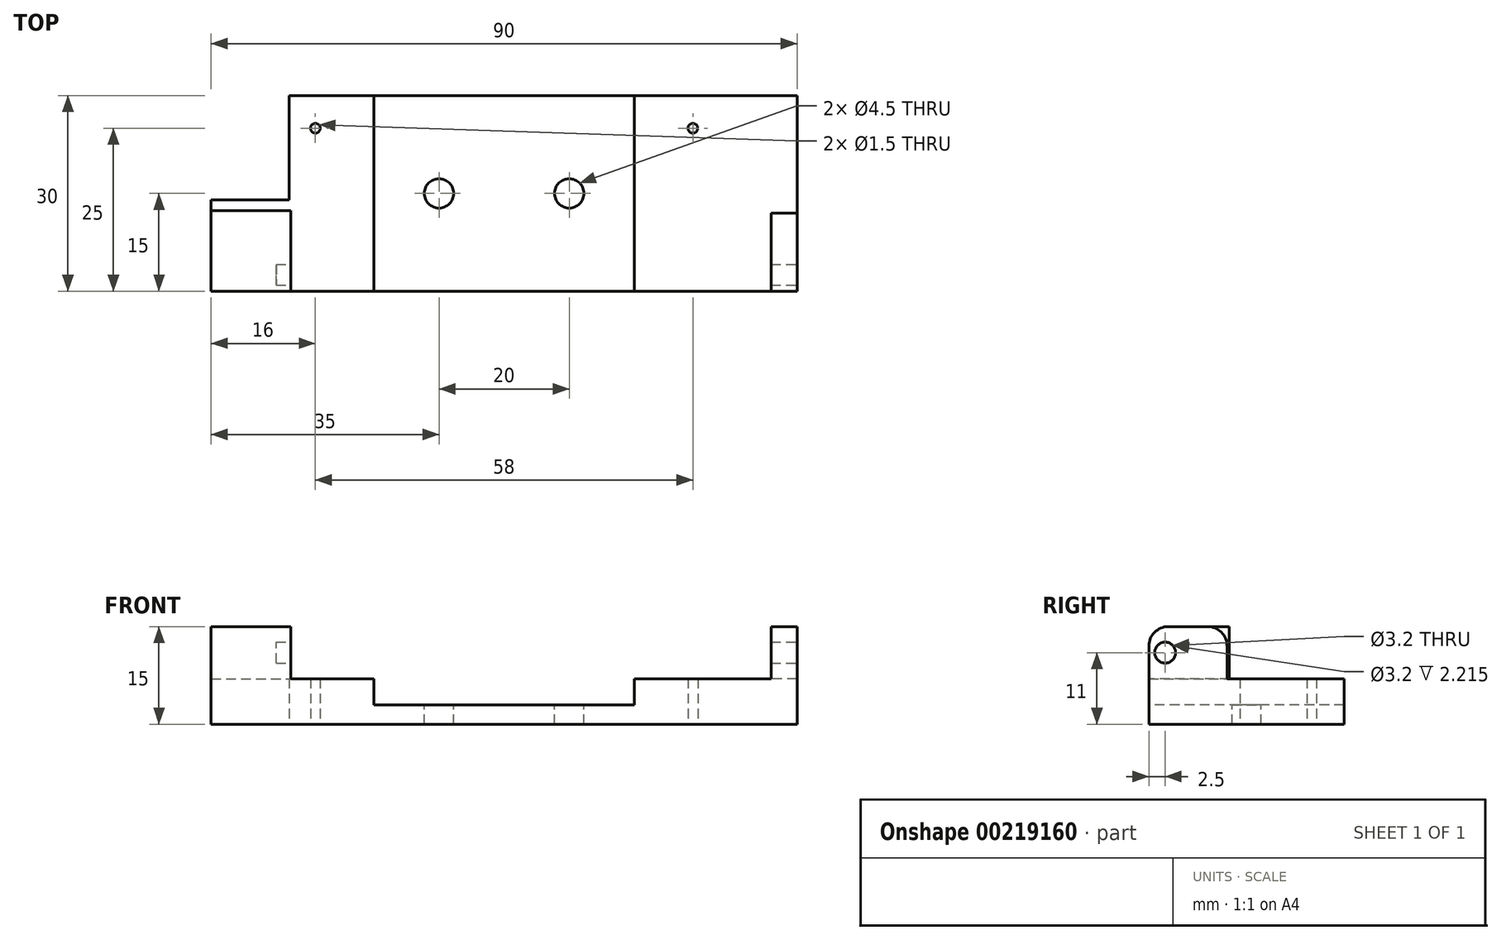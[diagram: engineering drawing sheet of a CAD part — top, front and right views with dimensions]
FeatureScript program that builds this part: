
annotation { "Feature Type Name" : "Feature", "Feature Type Description" : "" }
export const myFeature = defineFeature(function(context is Context, id is Id, definition is map)
    precondition{}
    {
        {
            var Q0;
            Q0=qCreatedBy(makeId("Top.planeOp"),FACE);
            var sketch = newSketch(context, id + "F0", { "sketchPlane" : qUnion([Q0])});
            skLineSegment(sketch, "E0.bottom", {"start": v(-45, 15) * mm, "end": v(45, 15) * mm});
            skLineSegment(sketch, "E0.top", {"start": v(-45, -15) * mm, "end": v(45, -15) * mm});
            skLineSegment(sketch, "E0.left", {"start": v(-45, 15) * mm, "end": v(-45, -15) * mm});
            skLineSegment(sketch, "E0.right", {"start": v(45, 15) * mm, "end": v(45, -15) * mm});
            skPoint(sketch, "E0.middle", {"position": v(0, 0) * mm});
            skLineSegment(sketch, "E1.bottom", {"start": v(-45, 15) * mm, "end": v(-33, 15) * mm});
            skLineSegment(sketch, "E1.top", {"start": v(-45, -1) * mm, "end": v(-33, -1) * mm});
            skLineSegment(sketch, "E1.left", {"start": v(-45, 15) * mm, "end": v(-45, -1) * mm});
            skLineSegment(sketch, "E1.right", {"start": v(-33, 15) * mm, "end": v(-33, -1) * mm});
            skLineSegment(sketch, "E2", {"start": v(45, 15) * mm, "end": v(29, 15) * mm});
            skLineSegment(sketch, "E3", {"start": v(29, 15) * mm, "end": v(29, 10) * mm});
            skLineSegment(sketch, "E4", {"start": v(-33, 15) * mm, "end": v(-29, 15) * mm});
            skLineSegment(sketch, "E5", {"start": v(-29, 15) * mm, "end": v(-29, 10) * mm});
            skCircle(sketch, "E6", {"center": v(-29, 10) * mm, "radius": 0.75 * mm});
            skCircle(sketch, "E7", {"center": v(29, 10) * mm, "radius": 0.75 * mm});
            skSolve(sketch);
        }
        {
            var Q0;
            Q0=makeQuery(id+"F0.imprint","IMPRINT",FACE,{"disambiguationData":[TD([[makeQuery(id+"F0.imprint","IMPRINT",EDGE,{"derivedFrom":sQuery(id+"F0.wireOp",EDGE,"E0.bottom")}),-1.0]])]});
            extrude(context, id + "F1", {"entities" : qUnion([Q0]), "depth" : 7 * mm});
        }
        {
            var Q0;
            Q0=makeQuery(id+"F1.opExtrude","CAP_FACE",FACE,{"disambiguationData":[OSD([sQuery(id+"F0.wireOp",EDGE,"E0.bottom"),sQuery(id+"F0.wireOp",EDGE,"E0.top"),sQuery(id+"F0.wireOp",EDGE,"E0.left"),sQuery(id+"F0.wireOp",EDGE,"E0.right"),sQuery(id+"F0.wireOp",EDGE,"E1.top"),sQuery(id+"F0.wireOp",EDGE,"E1.right"),sQuery(id+"F0.wireOp",EDGE,"E2"),sQuery(id+"F0.wireOp",EDGE,"E4"),sQuery(id+"F0.wireOp",EDGE,"E6"),sQuery(id+"F0.wireOp",EDGE,"E7")])],"isStart":false});
            var sketch = newSketch(context, id + "F2", { "sketchPlane" : qUnion([Q0])});
            skLineSegment(sketch, "E8.bottom", {"start": v(-45, -1) * mm, "end": v(-32.79, -1) * mm});
            skLineSegment(sketch, "E8.top", {"start": v(-45, -15) * mm, "end": v(-32.79, -15) * mm});
            skLineSegment(sketch, "E8.left", {"start": v(-45, -1) * mm, "end": v(-45, -15) * mm});
            skLineSegment(sketch, "E8.right", {"start": v(-32.79, -1) * mm, "end": v(-32.79, -15) * mm});
            skLineSegment(sketch, "E9.bottom", {"start": v(45, -15) * mm, "end": v(41, -15) * mm});
            skLineSegment(sketch, "E9.top", {"start": v(45, -3) * mm, "end": v(41, -3) * mm});
            skLineSegment(sketch, "E9.left", {"start": v(45, -15) * mm, "end": v(45, -3) * mm});
            skLineSegment(sketch, "E9.right", {"start": v(41, -15) * mm, "end": v(41, -3) * mm});
            skSolve(sketch);
        }
        {
            var Q0;
            Q0=makeQuery(id+"F2.imprint","IMPRINT",FACE,{"disambiguationData":[TD([[makeQuery(id+"F2.imprint","IMPRINT",EDGE,{"derivedFrom":sQuery(id+"F2.wireOp",EDGE,"E8.top")}),1.0]])]});
            var Q1;
            Q1=makeQuery(id+"F2.imprint","IMPRINT",FACE,{"disambiguationData":[TD([[makeQuery(id+"F2.imprint","IMPRINT",EDGE,{"derivedFrom":sQuery(id+"F2.wireOp",EDGE,"E9.bottom")}),1.0]])]});
            extrude(context, id + "F3", {"entities" : qUnion([Q0, Q1]), "operationType" : NewBodyOperationType.ADD, "depth" : 8 * mm});
        }
        {
            var Q0;
            Q0=makeQuery(id+"F3.opExtrude","CAP_FACE",FACE,{"disambiguationData":[OSD([sQuery(id+"F2.wireOp",EDGE,"E8.bottom"),sQuery(id+"F2.wireOp",EDGE,"E8.top"),sQuery(id+"F2.wireOp",EDGE,"E8.left"),sQuery(id+"F2.wireOp",EDGE,"E8.right")])],"isStart":false});
            var sketch = newSketch(context, id + "F4", { "sketchPlane" : qUnion([Q0])});
            skLineSegment(sketch, "E10.bottom", {"start": v(-45, -1) * mm, "end": v(-32.79, -1) * mm});
            skLineSegment(sketch, "E10.top", {"start": v(-45, -2.64) * mm, "end": v(-32.79, -2.64) * mm});
            skLineSegment(sketch, "E10.left", {"start": v(-45, -1) * mm, "end": v(-45, -2.64) * mm});
            skLineSegment(sketch, "E10.right", {"start": v(-32.79, -1) * mm, "end": v(-32.79, -2.64) * mm});
            skSolve(sketch);
        }
        {
            var Q0;
            Q0=qSketchRegion(id+"F4",true);
            extrude(context, id + "F5", {"entities" : qUnion([Q0]), "operationType" : NewBodyOperationType.REMOVE, "oppositeDirection" : true, "depth" : 8 * mm});
        }
        {
            var Q0;
            Q0=makeQuery(id+"F3.boolean.opBoolean","MERGE",FACE,{"derivedFrom":[makeQuery(id+"F1.opExtrude","SWEPT_FACE",FACE,{"disambiguationData":[OSD([sQuery(id+"F0.wireOp",EDGE,"E0.right")])]}),makeQuery(id+"F3.opExtrude","SWEPT_FACE",FACE,{"disambiguationData":[OSD([sQuery(id+"F2.wireOp",EDGE,"E9.left")])]})]});
            var sketch = newSketch(context, id + "F6", { "sketchPlane" : qUnion([Q0])});
            skLineSegment(sketch, "E11", {"start": v(-15, 7) * mm, "end": v(-12.5, 7) * mm});
            skLineSegment(sketch, "E12", {"start": v(-12.5, 7) * mm, "end": v(-12.5, 11) * mm});
            skCircle(sketch, "E13", {"center": v(-12.5, 11) * mm, "radius": 1.6 * mm});
            skSolve(sketch);
        }
        {
            var Q0;
            Q0=qSketchRegion(id+"F6",true);
            extrude(context, id + "F7", {"entities" : qUnion([Q0]), "operationType" : NewBodyOperationType.REMOVE, "oppositeDirection" : true, "depth" : 80 * mm});
        }
        {
            var Q0;
            Q0=makeQuery(id+"F5.boolean.opBoolean","MERGE",FACE,{"derivedFrom":[makeQuery(id+"F1.opExtrude","CAP_FACE",FACE,{"disambiguationData":[OSD([sQuery(id+"F0.wireOp",EDGE,"E0.bottom"),sQuery(id+"F0.wireOp",EDGE,"E0.top"),sQuery(id+"F0.wireOp",EDGE,"E0.left"),sQuery(id+"F0.wireOp",EDGE,"E0.right"),sQuery(id+"F0.wireOp",EDGE,"E1.top"),sQuery(id+"F0.wireOp",EDGE,"E1.right"),sQuery(id+"F0.wireOp",EDGE,"E2"),sQuery(id+"F0.wireOp",EDGE,"E4"),sQuery(id+"F0.wireOp",EDGE,"E6"),sQuery(id+"F0.wireOp",EDGE,"E7")])],"isStart":false}),makeQuery(id+"F5.opExtrude","CAP_FACE",FACE,{"disambiguationData":[OSD([sQuery(id+"F4.wireOp",EDGE,"E10.bottom"),sQuery(id+"F4.wireOp",EDGE,"E10.top"),sQuery(id+"F4.wireOp",EDGE,"E10.left"),sQuery(id+"F4.wireOp",EDGE,"E10.right")])],"isStart":false})]});
            var sketch = newSketch(context, id + "F8", { "sketchPlane" : qUnion([Q0])});
            skLineSegment(sketch, "E14", {"start": v(0, 0) * mm, "end": v(10, 0) * mm});
            skLineSegment(sketch, "E15", {"start": v(10, 0) * mm, "end": v(-10, 0) * mm});
            skPoint(sketch, "E15.endSnap0", {"position": v(5, 0) * mm});
            skCircle(sketch, "E16", {"center": v(-10, 0) * mm, "radius": 2.25 * mm});
            skCircle(sketch, "E17", {"center": v(10, 0) * mm, "radius": 2.25 * mm});
            skSolve(sketch);
        }
        {
            var Q0;
            Q0=makeQuery(id+"F8.imprint","IMPRINT",FACE,{"disambiguationData":[TD([[makeQuery(id+"F8.imprint","IMPRINT",EDGE,{"derivedFrom":sQuery(id+"F8.wireOp",EDGE,"E16")}),1.0]])]});
            var Q1;
            Q1=makeQuery(id+"F8.imprint","IMPRINT",FACE,{"disambiguationData":[TD([[makeQuery(id+"F8.imprint","IMPRINT",EDGE,{"derivedFrom":sQuery(id+"F8.wireOp",EDGE,"E17")}),1.0]])]});
            extrude(context, id + "F9", {"entities" : qUnion([Q0, Q1]), "operationType" : NewBodyOperationType.REMOVE, "oppositeDirection" : true, "depth" : 25 * mm});
        }
        {
            var Q0;
            Q0=makeQuery(id+"F5.boolean.opBoolean","MERGE",FACE,{"derivedFrom":[makeQuery(id+"F1.opExtrude","CAP_FACE",FACE,{"disambiguationData":[OSD([sQuery(id+"F0.wireOp",EDGE,"E0.bottom"),sQuery(id+"F0.wireOp",EDGE,"E0.top"),sQuery(id+"F0.wireOp",EDGE,"E0.left"),sQuery(id+"F0.wireOp",EDGE,"E0.right"),sQuery(id+"F0.wireOp",EDGE,"E1.top"),sQuery(id+"F0.wireOp",EDGE,"E1.right"),sQuery(id+"F0.wireOp",EDGE,"E2"),sQuery(id+"F0.wireOp",EDGE,"E4"),sQuery(id+"F0.wireOp",EDGE,"E6"),sQuery(id+"F0.wireOp",EDGE,"E7")])],"isStart":false}),makeQuery(id+"F5.opExtrude","CAP_FACE",FACE,{"disambiguationData":[OSD([sQuery(id+"F4.wireOp",EDGE,"E10.bottom"),sQuery(id+"F4.wireOp",EDGE,"E10.top"),sQuery(id+"F4.wireOp",EDGE,"E10.left"),sQuery(id+"F4.wireOp",EDGE,"E10.right")])],"isStart":false})]});
            var sketch = newSketch(context, id + "F10", { "sketchPlane" : qUnion([Q0])});
            skLineSegment(sketch, "E18.bottom", {"start": v(20, 15) * mm, "end": v(-20, 15) * mm});
            skLineSegment(sketch, "E18.top", {"start": v(20, -15) * mm, "end": v(-20, -15) * mm});
            skLineSegment(sketch, "E18.left", {"start": v(20, 15) * mm, "end": v(20, -15) * mm});
            skLineSegment(sketch, "E18.right", {"start": v(-20, 15) * mm, "end": v(-20, -15) * mm});
            skPoint(sketch, "E18.middle", {"position": v(0, 0) * mm});
            skSolve(sketch);
        }
        {
            var Q0;
            Q0=makeQuery(id+"F10.imprint","IMPRINT",FACE,{"disambiguationData":[TD([[makeQuery(id+"F10.imprint","IMPRINT",EDGE,{"derivedFrom":sQuery(id+"F10.wireOp",EDGE,"E18.bottom")}),-1.0]])]});
            extrude(context, id + "F11", {"entities" : qUnion([Q0]), "operationType" : NewBodyOperationType.REMOVE, "oppositeDirection" : true, "depth" : 4 * mm});
        }
        {
            var Q0;
            Q0=makeQuery(id+"F3.opExtrude","CAP_EDGE",EDGE,{"disambiguationData":[OSD([sQuery(id+"F2.wireOp",EDGE,"E8.top")])],"isStart":false});
            var Q1;
            Q1=makeQuery(id+"F3.opExtrude","CAP_EDGE",EDGE,{"disambiguationData":[OSD([sQuery(id+"F2.wireOp",EDGE,"E9.bottom")])],"isStart":false});
            var Q2;
            Q2=makeQuery(id+"F5.boolean.opBoolean","COPY",EDGE,{"derivedFrom":makeQuery(id+"F5.opExtrude","CAP_EDGE",EDGE,{"disambiguationData":[OSD([sQuery(id+"F4.wireOp",EDGE,"E10.top")])],"isStart":true})});
            var Q3;
            Q3=makeQuery(id+"F3.opExtrude","CAP_EDGE",EDGE,{"disambiguationData":[OSD([sQuery(id+"F2.wireOp",EDGE,"E9.top")])],"isStart":false});
            fillet(context, id + "F12", {"entities" : qUnion([Q0, Q1, Q2, Q3]), "radius" : 3 * mm, "tangentPropagation" : true, "allowEdgeOverflow" : false});
        }
    });
